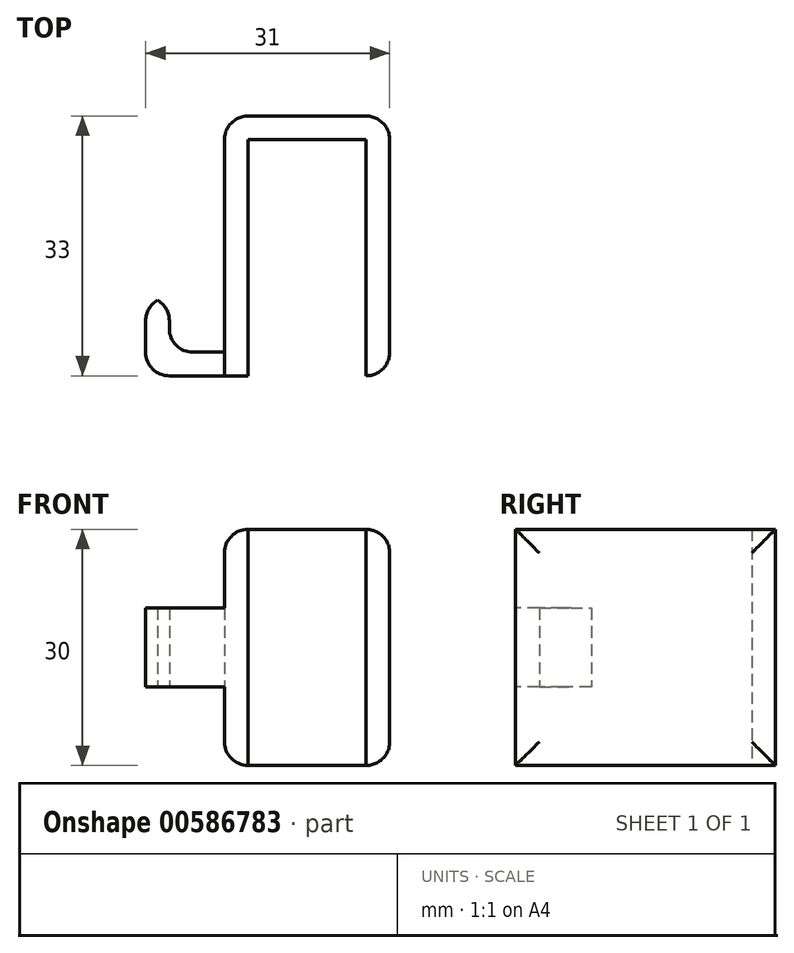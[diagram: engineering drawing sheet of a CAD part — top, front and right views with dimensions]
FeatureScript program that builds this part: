
annotation { "Feature Type Name" : "Feature", "Feature Type Description" : "" }
export const myFeature = defineFeature(function(context is Context, id is Id, definition is map)
    precondition{}
    {
        {
            var Q0;
            Q0=qCreatedBy(makeId("Top.planeOp"),FACE);
            var sketch = newSketch(context, id + "F0", { "sketchPlane" : qUnion([Q0])});
            skLineSegment(sketch, "E0", {"start": v(0, 0) * mm, "end": v(7.5, 0) * mm});
            skLineSegment(sketch, "E1", {"start": v(7.5, 0) * mm, "end": v(10.5, 0) * mm});
            skLineSegment(sketch, "E2", {"start": v(10.5, 0) * mm, "end": v(10.5, 33) * mm});
            skLineSegment(sketch, "E3", {"start": v(10.5, 33) * mm, "end": v(-10.5, 33) * mm});
            skLineSegment(sketch, "E4", {"start": v(-10.5, 33) * mm, "end": v(-10.5, 0) * mm});
            skLineSegment(sketch, "E5", {"start": v(-10.5, 0) * mm, "end": v(-7.5, 0) * mm});
            skLineSegment(sketch, "E6", {"start": v(-7.5, 0) * mm, "end": v(-7.5, 30) * mm});
            skLineSegment(sketch, "E7", {"start": v(-7.5, 30) * mm, "end": v(7.5, 30) * mm});
            skLineSegment(sketch, "E8", {"start": v(7.5, 30) * mm, "end": v(7.5, 0) * mm});
            skLineSegment(sketch, "E9", {"start": v(-10.5, 0) * mm, "end": v(-20.5, 0) * mm});
            skLineSegment(sketch, "E10", {"start": v(-20.5, 0) * mm, "end": v(-20.5, 10) * mm});
            skLineSegment(sketch, "E11", {"start": v(-20.5, 10) * mm, "end": v(-17.5, 10) * mm});
            skLineSegment(sketch, "E12", {"start": v(-17.5, 10) * mm, "end": v(-17.5, 3) * mm});
            skLineSegment(sketch, "E13", {"start": v(-17.5, 3) * mm, "end": v(-10.5, 3) * mm});
            skSolve(sketch);
        }
        {
            var Q0;
            Q0=makeQuery(id+"F0.imprint","IMPRINT",FACE,{"disambiguationData":[TD([[makeQuery(id+"F0.imprint","IMPRINT",EDGE,{"derivedFrom":sQuery(id+"F0.wireOp",EDGE,"E1")}),1.0]])]});
            extrude(context, id + "F1", {"entities" : qUnion([Q0]), "depth" : 30 * mm, "offsetDistance" : 25 * mm});
        }
        {
            var Q0;
            Q0 = qSketchRegion(id + "F0", true);
            extrude(context, id + "F2", {"entities" : qUnion([Q0]), "operationType" : NewBodyOperationType.ADD, "depth" : 20 * mm, "offsetDistance" : 25 * mm, "hasSecondDirection" : true, "secondDirectionOppositeDirection" : false, "secondDirectionDepth" : 10 * mm});
        }
        {
            var Q0;
            Q0=makeQuery(id+"F2.opExtrude","SWEPT_EDGE",EDGE,{"disambiguationData":[OSD([sQuery(id+"F0.wireOp",EDGE,"E4"),sQuery(id+"F0.wireOp",EDGE,"E13")])]});
            var Q1;
            Q1=makeQuery(id+"F2.opExtrude","SWEPT_EDGE",EDGE,{"disambiguationData":[OSD([sQuery(id+"F0.wireOp",EDGE,"E12"),sQuery(id+"F0.wireOp",EDGE,"E13")])]});
            var Q2;
            Q2=makeQuery(id+"F2.opExtrude","SWEPT_EDGE",EDGE,{"disambiguationData":[OSD([sQuery(id+"F0.wireOp",EDGE,"E11"),sQuery(id+"F0.wireOp",EDGE,"E12")])]});
            var Q3;
            Q3=makeQuery(id+"F2.opExtrude","SWEPT_EDGE",EDGE,{"disambiguationData":[OSD([sQuery(id+"F0.wireOp",EDGE,"E9"),sQuery(id+"F0.wireOp",EDGE,"E10")])]});
            var Q4;
            Q4=makeQuery(id+"F2.opExtrude","SWEPT_EDGE",EDGE,{"disambiguationData":[OSD([sQuery(id+"F0.wireOp",EDGE,"E10"),sQuery(id+"F0.wireOp",EDGE,"E11")])]});
            var Q5;
            Q5=makeQuery(id+"F1.opExtrude","CAP_EDGE",EDGE,{"disambiguationData":[OSD([sQuery(id+"F0.wireOp",EDGE,"E4")])],"isStart":false});
            var Q6;
            Q6=makeQuery(id+"F1.opExtrude","SWEPT_FACE",FACE,{"disambiguationData":[OSD([sQuery(id+"F0.wireOp",EDGE,"E2")])]});
            var Q7;
            Q7=makeQuery(id+"F1.opExtrude","SWEPT_EDGE",EDGE,{"disambiguationData":[OSD([sQuery(id+"F0.wireOp",EDGE,"E1"),sQuery(id+"F0.wireOp",EDGE,"E2")])]});
            var Q8;
            Q8=makeQuery(id+"F1.opExtrude","CAP_EDGE",EDGE,{"disambiguationData":[OSD([sQuery(id+"F0.wireOp",EDGE,"E4")])],"isStart":true});
            var Q9;
            Q9=makeQuery(id+"F1.opExtrude","SWEPT_EDGE",EDGE,{"disambiguationData":[OSD([sQuery(id+"F0.wireOp",EDGE,"E3"),sQuery(id+"F0.wireOp",EDGE,"E4")])]});
            fillet(context, id + "F3", {"entities" : qUnion([Q0, Q1, Q2, Q3, Q4, Q5, Q6, Q7, Q8, Q9]), "radius" : 3 * mm, "tangentPropagation" : true, "allowEdgeOverflow" : false});
        }
    });
